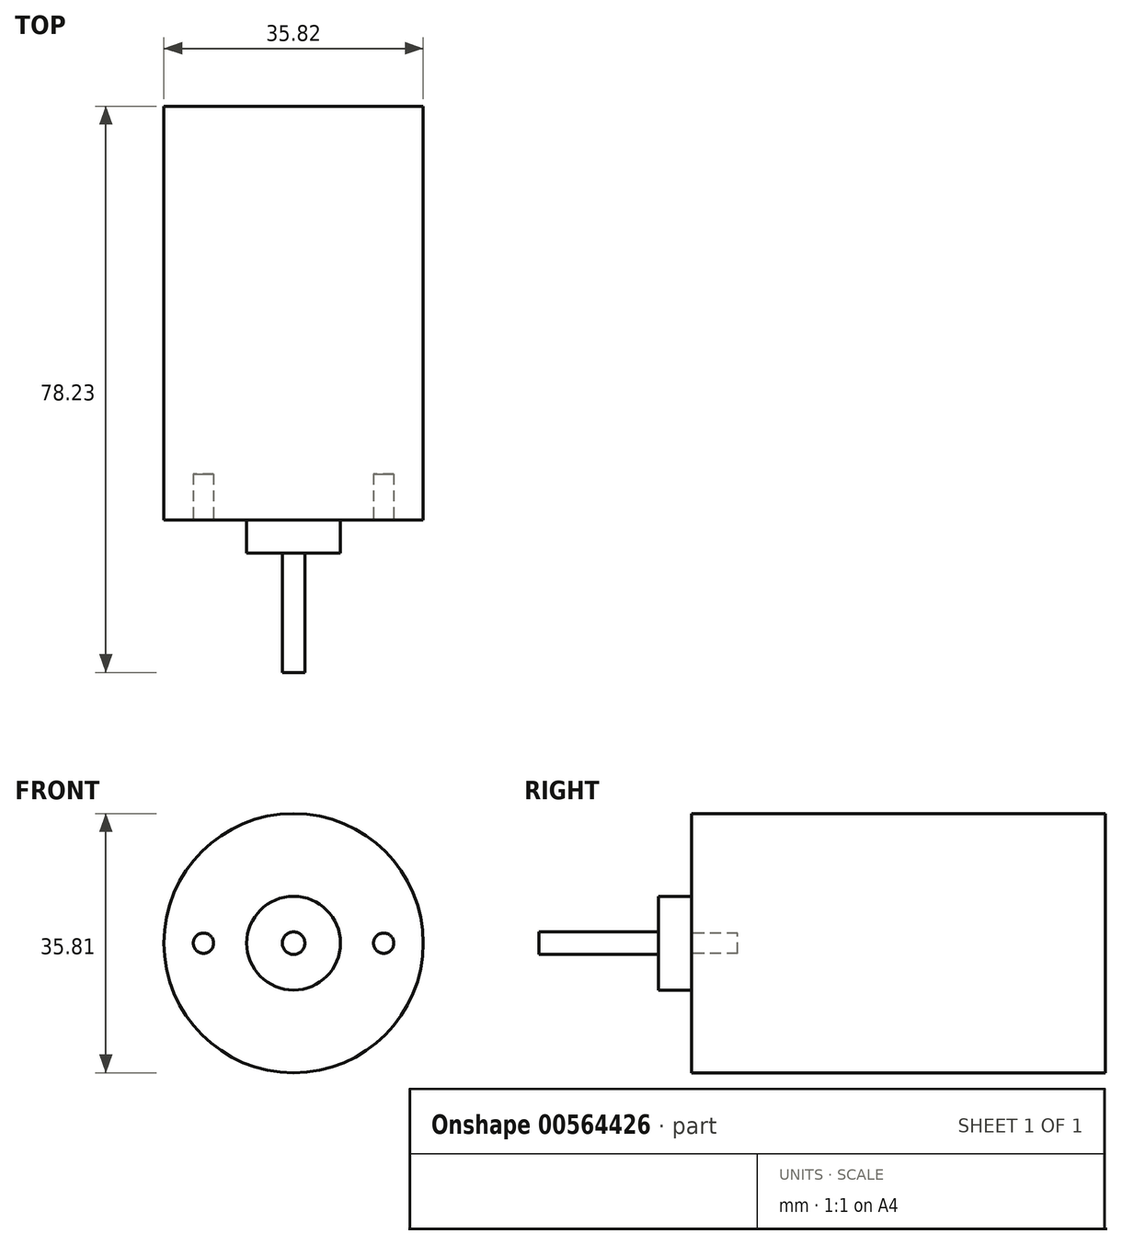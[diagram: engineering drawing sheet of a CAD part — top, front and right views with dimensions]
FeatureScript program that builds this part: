
annotation { "Feature Type Name" : "Feature", "Feature Type Description" : "" }
export const myFeature = defineFeature(function(context is Context, id is Id, definition is map)
    precondition{}
    {
        {
            var Q0;
            Q0=qCreatedBy(makeId("Right.planeOp"),FACE);
            var sketch = newSketch(context, id + "F0", { "sketchPlane" : qUnion([Q0])});
            skLineSegment(sketch, "E0", {"start": v(3.87, -3.78) * mm, "end": v(-74.36, -3.78) * mm});
            skLineSegment(sketch, "E1", {"start": v(-74.36, -3.78) * mm, "end": v(-74.36, -2.21) * mm});
            skLineSegment(sketch, "E2", {"start": v(-74.36, -2.21) * mm, "end": v(-57.85, -2.21) * mm});
            skLineSegment(sketch, "E3", {"start": v(-57.85, -2.21) * mm, "end": v(-57.85, 2.7) * mm});
            skLineSegment(sketch, "E4", {"start": v(-57.85, 2.7) * mm, "end": v(-53.28, 2.7) * mm});
            skLineSegment(sketch, "E5", {"start": v(-53.28, 2.7) * mm, "end": v(-53.28, 14.13) * mm});
            skLineSegment(sketch, "E6", {"start": v(-53.28, 14.13) * mm, "end": v(3.87, 14.13) * mm});
            skLineSegment(sketch, "E7", {"start": v(3.87, 14.13) * mm, "end": v(3.87, -3.78) * mm});
            skSolve(sketch);
        }
        {
            var Q0;
            Q0=makeQuery(id+"F0.imprint","IMPRINT",FACE,{"disambiguationData":[TD([[makeQuery(id+"F0.imprint","IMPRINT",EDGE,{"derivedFrom":sQuery(id+"F0.wireOp",EDGE,"E0")}),-1.0]])]});
            var Q1;
            Q1=sQuery(id+"F0.wireOp",EDGE,"E0");
            revolve(context, id + "F1", {"entities" : qUnion([Q0]), "axis" : qUnion([Q1]), "revolveType" : RevolveType.FULL});
        }
        {
            var Q0;
            Q0=makeQuery(id+"F1.opRevolve","SWEPT_FACE",FACE,{"disambiguationData":[OSD([sQuery(id+"F0.wireOp",EDGE,"E5")])]});
            var sketch = newSketch(context, id + "F2", { "sketchPlane" : qUnion([Q0])});
            skCircle(sketch, "E8.0", {"center": v(0, -3.78) * mm, "radius": 1.56 * mm, "construction": true});
            skCircle(sketch, "E9", {"center": v(12.45, -3.78) * mm, "radius": 1.4 * mm});
            skCircle(sketch, "E10", {"center": v(-12.45, -3.78) * mm, "radius": 1.4 * mm});
            skLineSegment(sketch, "E11", {"start": v(12.45, -3.78) * mm, "end": v(-12.45, -3.78) * mm, "construction": true});
            skSolve(sketch);
        }
        {
            var Q0;
            Q0 = qSketchRegion(id + "F2", true);
            extrude(context, id + "F3", {"entities" : qUnion([Q0]), "operationType" : NewBodyOperationType.REMOVE, "oppositeDirection" : true, "depth" : 6.35 * mm, "offsetDistance" : 25.4 * mm});
        }
    });
